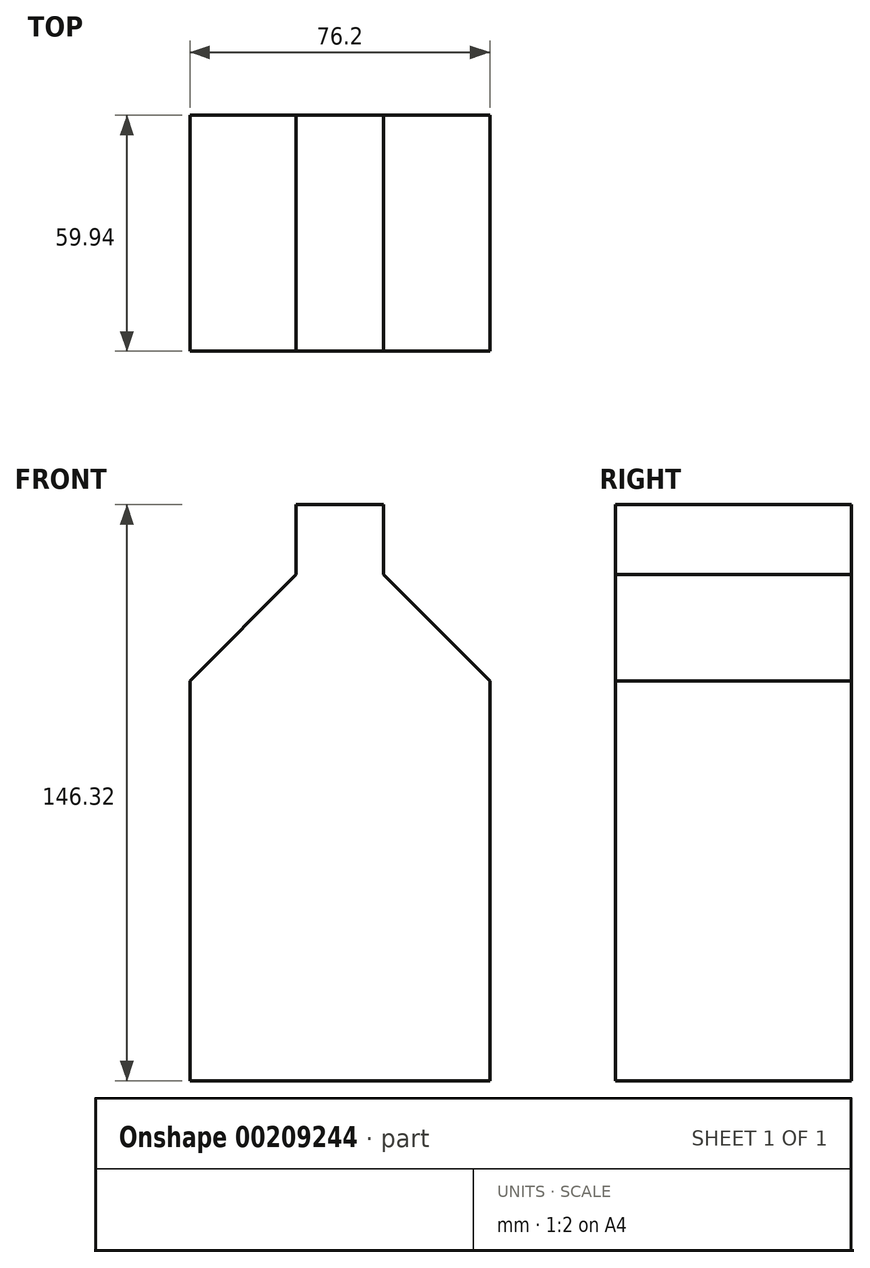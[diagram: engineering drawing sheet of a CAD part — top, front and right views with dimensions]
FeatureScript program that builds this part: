
annotation { "Feature Type Name" : "Feature", "Feature Type Description" : "" }
export const myFeature = defineFeature(function(context is Context, id is Id, definition is map)
    precondition{}
    {
        {
            var Q0;
            Q0=qCreatedBy(makeId("Front.planeOp"),FACE);
            var sketch = newSketch(context, id + "F0", { "sketchPlane" : qUnion([Q0])});
            skLineSegment(sketch, "E0.top", {"start": v(38.1, -87.83) * mm, "end": v(-38.1, -87.83) * mm});
            skLineSegment(sketch, "E0.left", {"start": v(38.1, 13.77) * mm, "end": v(38.1, -87.83) * mm});
            skLineSegment(sketch, "E0.right", {"start": v(-38.1, 13.77) * mm, "end": v(-38.1, -87.83) * mm});
            skPoint(sketch, "E0.middle", {"position": v(0, -37.03) * mm});
            skLineSegment(sketch, "E1", {"start": v(-38.1, 13.77) * mm, "end": v(-11.16, 40.7) * mm});
            skLineSegment(sketch, "E2", {"start": v(-11.16, 40.7) * mm, "end": v(-11.16, 58.49) * mm});
            skLineSegment(sketch, "E3", {"start": v(-11.16, 58.49) * mm, "end": v(0, 58.49) * mm});
            skLineSegment(sketch, "E4.MirrorCS", {"start": v(11.16, 58.49) * mm, "end": v(0, 58.49) * mm});
            skLineSegment(sketch, "E5.MirrorCS", {"start": v(11.16, 40.7) * mm, "end": v(11.16, 58.49) * mm});
            skLineSegment(sketch, "E6.MirrorCS", {"start": v(38.1, 13.77) * mm, "end": v(11.16, 40.7) * mm});
            skSolve(sketch);
        }
        {
            var Q0;
            Q0=makeQuery(id+"F0.imprint","IMPRINT",FACE,{"disambiguationData":[TD([[makeQuery(id+"F0.imprint","IMPRINT",EDGE,{"derivedFrom":sQuery(id+"F0.wireOp",EDGE,"E0.top")}),-1.0]])]});
            extrude(context, id + "F1", {"entities" : qUnion([Q0]), "endBound" : BoundingType.SYMMETRIC, "depth" : 59.94 * mm});
        }
    });
